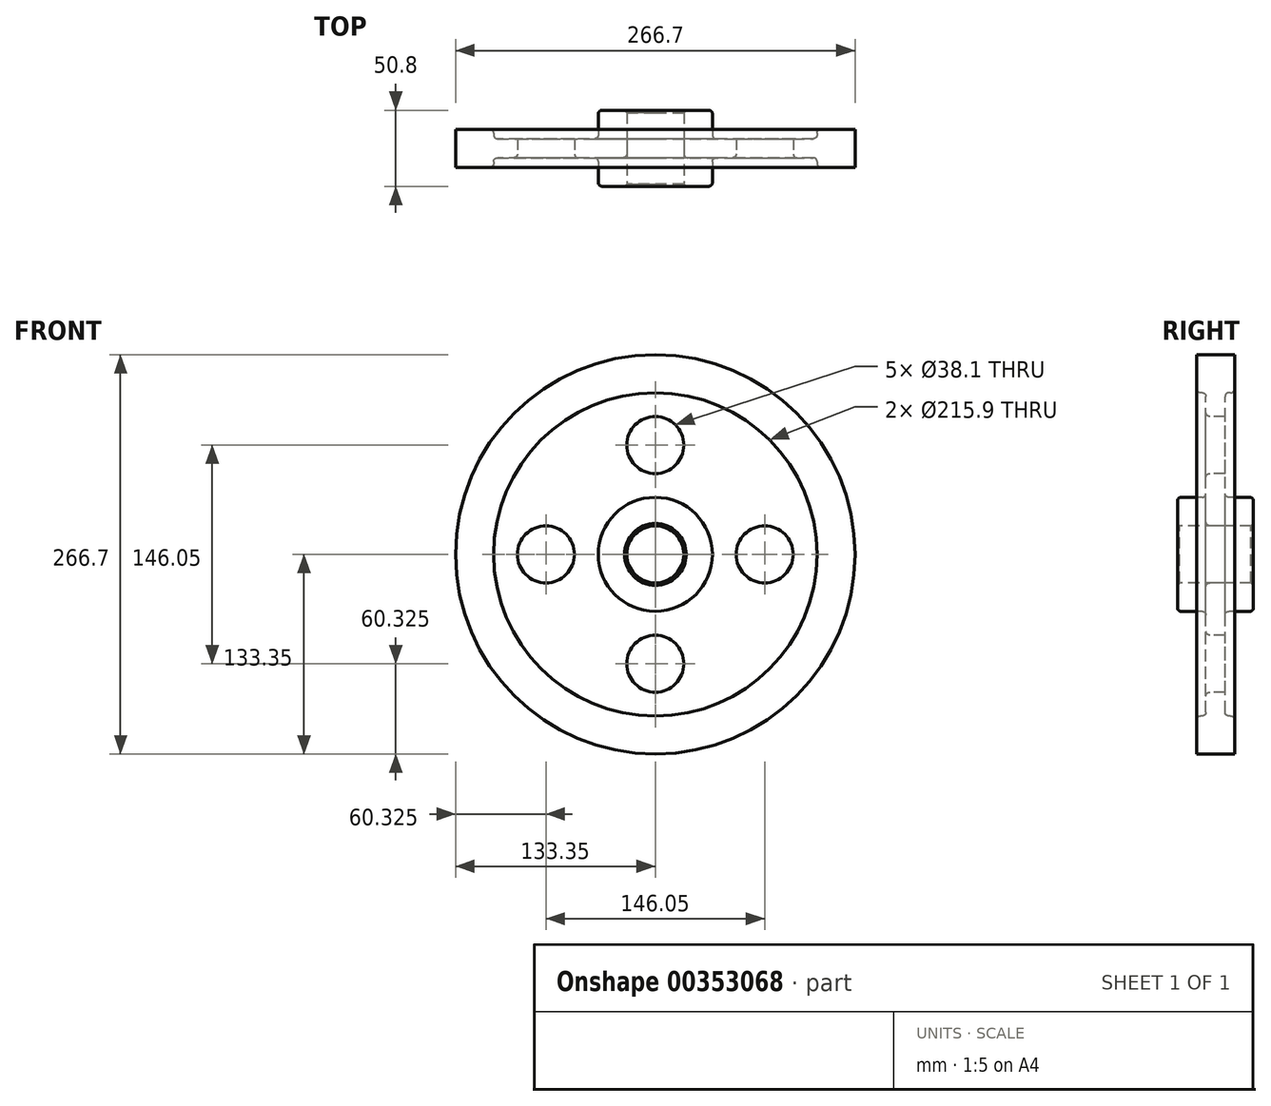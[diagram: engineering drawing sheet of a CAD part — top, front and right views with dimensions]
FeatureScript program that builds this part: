
annotation { "Feature Type Name" : "Feature", "Feature Type Description" : "" }
export const myFeature = defineFeature(function(context is Context, id is Id, definition is map)
    precondition{}
    {
        {
            var Q0;
            Q0=qCreatedBy(makeId("Right.planeOp"),FACE);
            var sketch = newSketch(context, id + "F0", { "sketchPlane" : qUnion([Q0])});
            skLineSegment(sketch, "E0", {"start": v(0, 0) * mm, "end": v(75.9, 0) * mm, "construction": true});
            skLineSegment(sketch, "E1.0", {"start": v(0, 19.05) * mm, "end": v(25.4, 19.05) * mm});
            skLineSegment(sketch, "E2.0", {"start": v(6.35, 38.1) * mm, "end": v(25.4, 38.1) * mm});
            skLineSegment(sketch, "E3.0", {"start": v(6.35, 107.95) * mm, "end": v(12.7, 107.95) * mm});
            skLineSegment(sketch, "E4.0", {"start": v(0, 133.35) * mm, "end": v(12.7, 133.35) * mm});
            skLineSegment(sketch, "E5", {"start": v(0, 0) * mm, "end": v(0, 133.35) * mm, "construction": true});
            skLineSegment(sketch, "E6.0", {"start": v(25.4, -1.38) * mm, "end": v(25.4, 0) * mm});
            skLineSegment(sketch, "E7.trimOffspring", {"start": v(12.7, 107.95) * mm, "end": v(12.7, 133.35) * mm});
            skLineSegment(sketch, "E8.trimOffspring", {"start": v(6.35, 38.1) * mm, "end": v(6.35, 107.95) * mm});
            skLineSegment(sketch, "E9.trimOffspring", {"start": v(25.4, 19.05) * mm, "end": v(25.4, 38.1) * mm});
            skLineSegment(sketch, "E10.MirrorCS", {"start": v(0, 133.35) * mm, "end": v(-12.7, 133.35) * mm});
            skLineSegment(sketch, "E11.MirrorCS", {"start": v(-12.7, 107.95) * mm, "end": v(-12.7, 133.35) * mm});
            skLineSegment(sketch, "E12.MirrorCS", {"start": v(-6.35, 107.95) * mm, "end": v(-12.7, 107.95) * mm});
            skLineSegment(sketch, "E13.MirrorCS", {"start": v(-6.35, 38.1) * mm, "end": v(-6.35, 107.95) * mm});
            skLineSegment(sketch, "E14.MirrorCS", {"start": v(-6.35, 38.1) * mm, "end": v(-25.4, 38.1) * mm});
            skLineSegment(sketch, "E15.MirrorCS", {"start": v(-25.4, 19.05) * mm, "end": v(-25.4, 38.1) * mm});
            skLineSegment(sketch, "E16.MirrorCS", {"start": v(0, 19.05) * mm, "end": v(-25.4, 19.05) * mm});
            skSolve(sketch);
        }
        {
            var Q0;
            Q0=makeQuery(id+"F0.imprint","IMPRINT",FACE,{"disambiguationData":[TD([[makeQuery(id+"F0.imprint","IMPRINT",EDGE,{"derivedFrom":sQuery(id+"F0.wireOp",EDGE,"E1.0")}),1.0]])]});
            var Q1;
            Q1=sQuery(id+"F0.wireOp",EDGE,"E0");
            revolve(context, id + "F1", {"entities" : qUnion([Q0]), "axis" : qUnion([Q1]), "revolveType" : RevolveType.FULL});
        }
        {
            var Q0;
            Q0=makeQuery(id+"F1.opRevolve","SWEPT_FACE",FACE,{"disambiguationData":[OSD([sQuery(id+"F0.wireOp",EDGE,"E13.MirrorCS")])]});
            var sketch = newSketch(context, id + "F2", { "sketchPlane" : qUnion([Q0])});
            skLineSegment(sketch, "E17", {"start": v(0, 0) * mm, "end": v(0, 73.03) * mm});
            skCircle(sketch, "E18", {"center": v(0, 73.03) * mm, "radius": 19.05 * mm});
            skCircle(sketch, "E19.1.0", {"center": v(-73.03, 0) * mm, "radius": 19.05 * mm});
            skCircle(sketch, "E19.2.0", {"center": v(0, -73.03) * mm, "radius": 19.05 * mm});
            skCircle(sketch, "E19.3.0", {"center": v(73.03, 0) * mm, "radius": 19.05 * mm});
            skPoint(sketch, "E19.center", {"position": v(0, 0) * mm});
            skSolve(sketch);
        }
        {
            var Q0;
            Q0=makeQuery(id+"F2.imprint","IMPRINT",FACE,{"disambiguationData":[TD([[makeQuery(id+"F2.imprint","IMPRINT",EDGE,{"derivedFrom":sQuery(id+"F2.wireOp",EDGE,"E18")}),1.0]])]});
            var Q1;
            Q1=makeQuery(id+"F2.imprint","IMPRINT",FACE,{"disambiguationData":[TD([[makeQuery(id+"F2.imprint","IMPRINT",EDGE,{"derivedFrom":sQuery(id+"F2.wireOp",EDGE,"E19.1.0")}),1.0]])]});
            var Q2;
            Q2=makeQuery(id+"F2.imprint","IMPRINT",FACE,{"disambiguationData":[TD([[makeQuery(id+"F2.imprint","IMPRINT",EDGE,{"derivedFrom":sQuery(id+"F2.wireOp",EDGE,"E19.2.0")}),1.0]])]});
            var Q3;
            Q3=makeQuery(id+"F2.imprint","IMPRINT",FACE,{"disambiguationData":[TD([[makeQuery(id+"F2.imprint","IMPRINT",EDGE,{"derivedFrom":sQuery(id+"F2.wireOp",EDGE,"E19.3.0")}),1.0]])]});
            extrude(context, id + "F3", {"entities" : qUnion([Q0, Q1, Q2, Q3]), "operationType" : NewBodyOperationType.REMOVE, "oppositeDirection" : true, "depth" : 25.4 * mm});
        }
        {
            var Q0;
            Q0=makeQuery(id+"F1.opRevolve","SWEPT_EDGE",EDGE,{"disambiguationData":[OSD([sQuery(id+"F0.wireOp",EDGE,"E14.MirrorCS"),sQuery(id+"F0.wireOp",EDGE,"E15.MirrorCS")])]});
            var Q1;
            Q1=makeQuery(id+"F1.opRevolve","SWEPT_EDGE",EDGE,{"disambiguationData":[OSD([sQuery(id+"F0.wireOp",EDGE,"E13.MirrorCS"),sQuery(id+"F0.wireOp",EDGE,"E14.MirrorCS")])]});
            var Q2;
            Q2=makeQuery(id+"F1.opRevolve","SWEPT_FACE",FACE,{"disambiguationData":[OSD([sQuery(id+"F0.wireOp",EDGE,"E13.MirrorCS")])]});
            var Q3;
            Q3=makeQuery(id+"F1.opRevolve","SWEPT_EDGE",EDGE,{"disambiguationData":[OSD([sQuery(id+"F0.wireOp",EDGE,"E11.MirrorCS"),sQuery(id+"F0.wireOp",EDGE,"E12.MirrorCS")])]});
            var Q4;
            Q4=makeQuery(id+"F1.opRevolve","SWEPT_EDGE",EDGE,{"disambiguationData":[OSD([sQuery(id+"F0.wireOp",EDGE,"E2.0"),sQuery(id+"F0.wireOp",EDGE,"E8.trimOffspring")])]});
            var Q5;
            Q5=makeQuery(id+"F1.opRevolve","SWEPT_EDGE",EDGE,{"disambiguationData":[OSD([sQuery(id+"F0.wireOp",EDGE,"E2.0"),sQuery(id+"F0.wireOp",EDGE,"E9.trimOffspring")])]});
            var Q6;
            Q6=makeQuery(id+"F1.opRevolve","SWEPT_FACE",FACE,{"disambiguationData":[OSD([sQuery(id+"F0.wireOp",EDGE,"E3.0")])]});
            var Q7;
            Q7=makeQuery(id+"F1.opRevolve","SWEPT_EDGE",EDGE,{"disambiguationData":[OSD([sQuery(id+"F0.wireOp",EDGE,"E3.0"),sQuery(id+"F0.wireOp",EDGE,"E7.trimOffspring")])]});
            var Q8;
            Q8=makeQuery(id+"F1.opRevolve","SWEPT_EDGE",EDGE,{"disambiguationData":[OSD([sQuery(id+"F0.wireOp",EDGE,"E3.0"),sQuery(id+"F0.wireOp",EDGE,"E8.trimOffspring")])]});
            fillet(context, id + "F4", {"entities" : qUnion([Q0, Q1, Q2, Q3, Q4, Q5, Q6, Q7, Q8]), "radius" : 2.54 * mm, "tangentPropagation" : true, "allowEdgeOverflow" : false});
        }
        {
            var Q0;
            Q0=makeQuery(id+"F1.opRevolve","SWEPT_EDGE",EDGE,{"disambiguationData":[OSD([sQuery(id+"F0.wireOp",EDGE,"E1.0"),sQuery(id+"F0.wireOp",EDGE,"E9.trimOffspring")])]});
            var Q1;
            Q1=makeQuery(id+"F1.opRevolve","SWEPT_FACE",FACE,{"disambiguationData":[OSD([sQuery(id+"F0.wireOp",EDGE,"E1.0"),sQuery(id+"F0.wireOp",EDGE,"E16.MirrorCS")])]});
            chamfer(context, id + "F5", {"entities" : qUnion([Q0, Q1]), "width" : 1.59 * mm, "tangentPropagation" : true});
        }
    });
